# Revit family: CabDoor_Raised_Colonial
name_source: partatom
category: Casework
units: mm (PartAtom-declared; Revit-internal decimal feet)

## family parameters
Always vertical = Yes
Classification Number = 23.40.35.11.11
Cut with Voids When Loaded = No
Room Calculation Point = No
Shared = No
Work Plane-Based = No

## types (1)
- CabDoor_Raised_Colonial
    Assembly Code = C1030410
    Bead Diameter = 0' - 1"
    Construction Details = http://www.arcat.com
    Corner Tenon Material = ARCAT - Wood - Walnut_Black
    Corner Tenon Placement = 0' - 0 3/4"
    Default Elevation = 0' - 0"
    Depth = 0' - 0 3/4"
    Description = Colonial Raised Panel Cabinet Door
    Expected Lifespan (Years) = 30
    Frame Material = ARCAT - Wood - Cherry_Brazillian
    Frame Width = 0' - 2"
    Green Building-LEED = http://www.arcat.com
    Height = 2' - 0"
    Keynote = 12350
    Maintenance Schedule (Months) = 24
    Manufacturer = Generic
    Manufacturer Fax = (203) 929-2444
    Manufacturer Website = http://www.arcat.com
    Model = Generic
    Panel Material = ARCAT - Wood - Walnut_Black
    Product Data = http://www.arcat.com
    Product Properties = http://www.arcat.com
    Specification = http://www.arcat.com
    Warranty Duration (Years) = 10
    Width = 2' - 10"

## geometry (parser evidence)
native form markers: Blend x3, Sweep x5
no freeform markers — native parametric forms only
